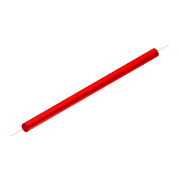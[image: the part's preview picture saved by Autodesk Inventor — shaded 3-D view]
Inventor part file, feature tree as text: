
AUTODESK INVENTOR PART (.ipt)
format: ipt  version: unknown  size: 156,160 bytes
history: native  units: in
note: dims shown in document units (in); Inventor stores cm internally (conversion verified against a paired STEP export)
features: extrude x1, other x1, sketch x1
ambient origin geometry x8: Origin, YZ Plane, XZ Plane, XY Plane, X Axis, Y Axis, Z Axis, Center Point
feature tree (3):
  extrude  "Extrusion5"  Depth=0.7874in TaperAngle=0.0deg
  other  "Work Axis7"
  sketch  "Sketch15"  dims[d33=0.0394in d34=0.7874in d35=0.0in]
